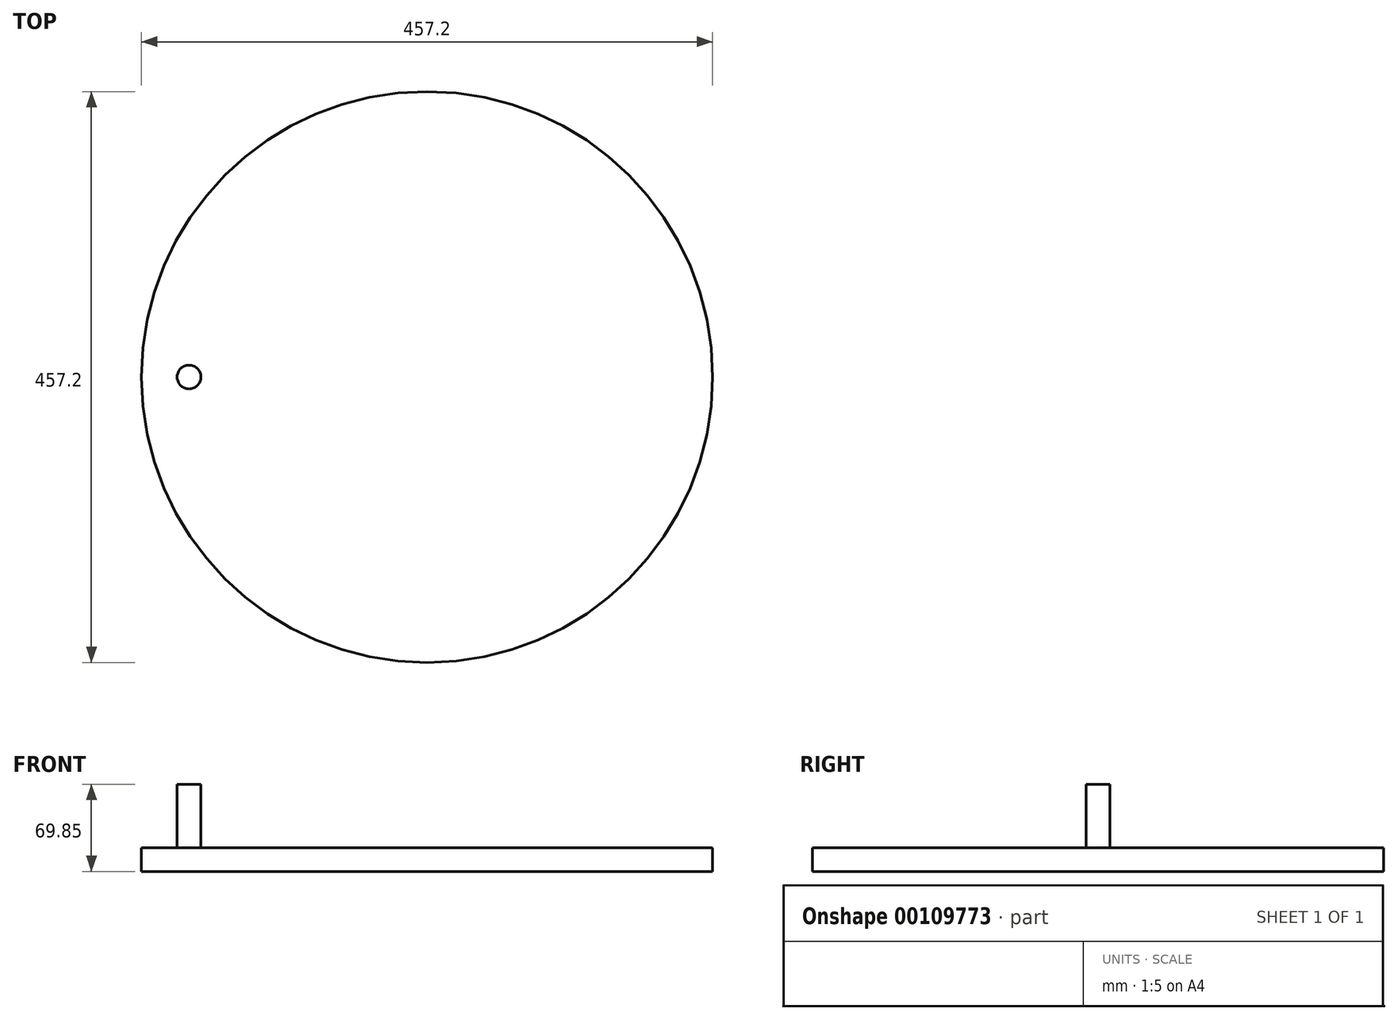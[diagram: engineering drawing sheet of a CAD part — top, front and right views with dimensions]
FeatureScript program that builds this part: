
annotation { "Feature Type Name" : "Feature", "Feature Type Description" : "" }
export const myFeature = defineFeature(function(context is Context, id is Id, definition is map)
    precondition{}
    {
        {
            var Q0;
            Q0=qCreatedBy(makeId("Top.planeOp"),FACE);
            var sketch = newSketch(context, id + "F0", { "sketchPlane" : qUnion([Q0])});
            skCircle(sketch, "E0", {"center": v(0, 0) * mm, "radius": 228.6 * mm});
            skSolve(sketch);
        }
        {
            var Q0;
            Q0=makeQuery(id+"F0.imprint","IMPRINT",FACE,{"disambiguationData":[TD([[makeQuery(id+"F0.imprint","IMPRINT",EDGE,{"derivedFrom":sQuery(id+"F0.wireOp",EDGE,"E0")}),1.0]])]});
            extrude(context, id + "F1", {"entities" : qUnion([Q0]), "depth" : 19.05 * mm});
        }
        {
            var Q0;
            Q0=makeQuery(id+"F1.opExtrude","CAP_FACE",FACE,{"disambiguationData":[OSD([sQuery(id+"F0.wireOp",EDGE,"E0")])],"isStart":false});
            var sketch = newSketch(context, id + "F2", { "sketchPlane" : qUnion([Q0])});
            skCircle(sketch, "E1", {"center": v(-190.5, 0) * mm, "radius": 9.52 * mm});
            skCircle(sketch, "E2", {"center": v(0, 0) * mm, "radius": 161.93 * mm, "construction": true});
            skSolve(sketch);
        }
        {
            var Q0;
            Q0 = qSketchRegion(id + "F2", true);
            extrude(context, id + "F3", {"entities" : qUnion([Q0]), "operationType" : NewBodyOperationType.ADD, "depth" : 50.8 * mm});
        }
    });
